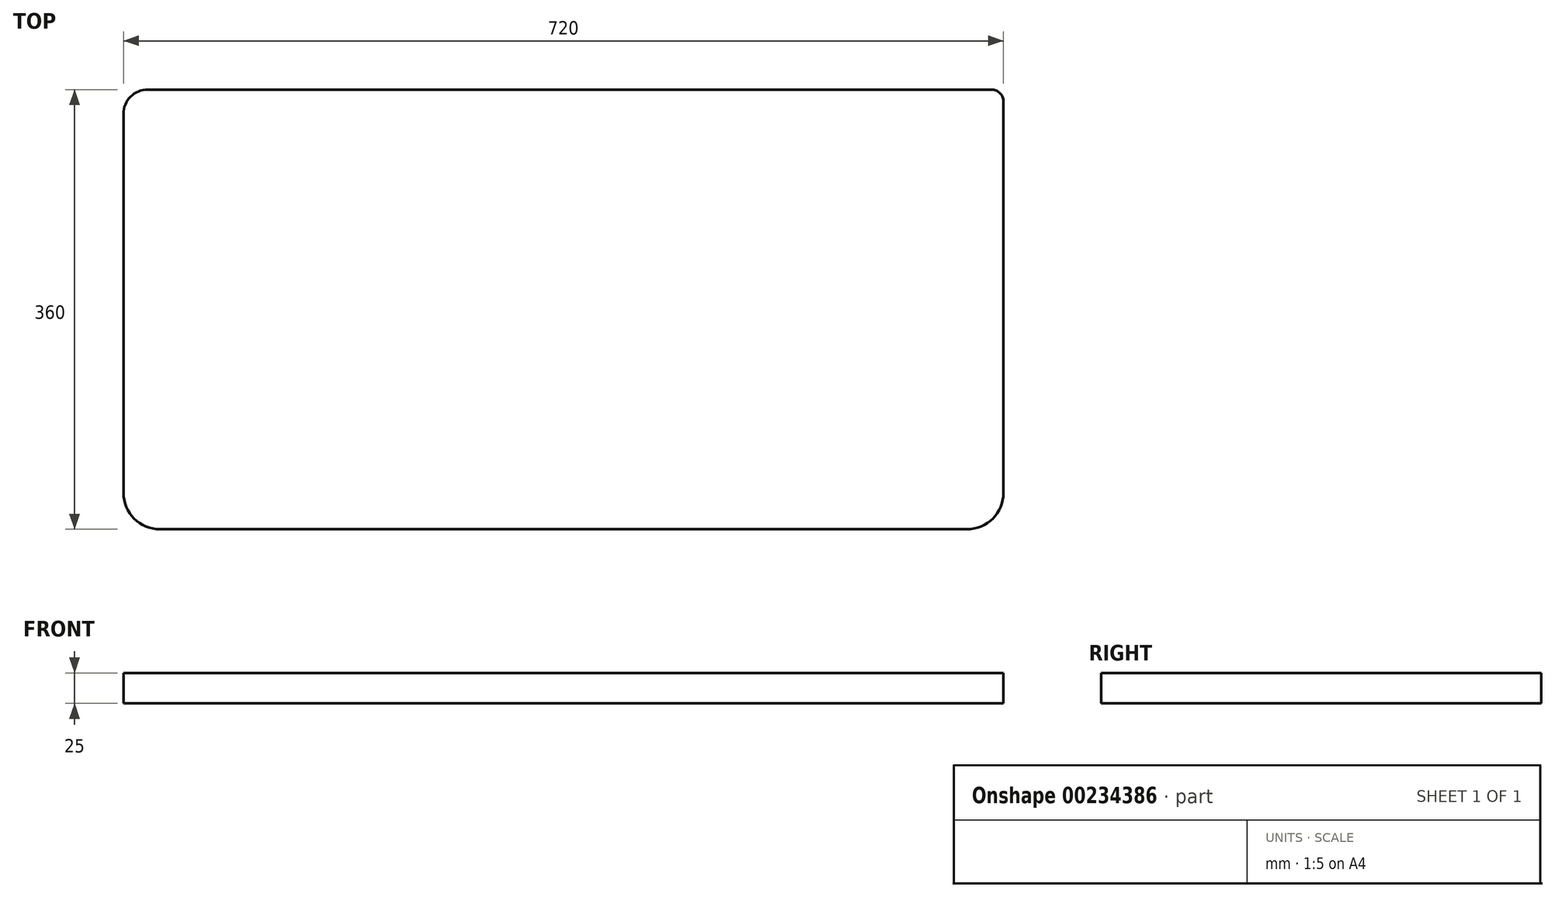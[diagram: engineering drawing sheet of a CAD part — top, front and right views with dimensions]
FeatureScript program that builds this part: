
annotation { "Feature Type Name" : "Feature", "Feature Type Description" : "" }
export const myFeature = defineFeature(function(context is Context, id is Id, definition is map)
    precondition{}
    {
        {
            var Q0;
            Q0=qCreatedBy(makeId("Top.planeOp"),FACE);
            var sketch = newSketch(context, id + "F0", { "sketchPlane" : qUnion([Q0])});
            skLineSegment(sketch, "E0.bottom", {"start": v(-340, 180) * mm, "end": v(350, 180) * mm});
            skLineSegment(sketch, "E0.top", {"start": v(-330, -180) * mm, "end": v(330, -180) * mm});
            skLineSegment(sketch, "E0.left", {"start": v(-360, 160) * mm, "end": v(-360, -150) * mm});
            skLineSegment(sketch, "E0.right", {"start": v(360, 170) * mm, "end": v(360, -150) * mm});
            skPoint(sketch, "E0.middle", {"position": v(0, 0) * mm});
            skPoint(sketch, "E1.visualSharp", {"position": v(-360, -180) * mm});
            skArc(sketch, "E1.filletArc", {"start": v(-360, -150) * mm, "mid": v(-351.21, -171.21) * mm, "end": v(-330, -180) * mm});
            skPoint(sketch, "E2.visualSharp", {"position": v(360, -180) * mm});
            skArc(sketch, "E2.filletArc", {"start": v(330, -180) * mm, "mid": v(351.21, -171.21) * mm, "end": v(360, -150) * mm});
            skPoint(sketch, "E3.visualSharp", {"position": v(-360, 180) * mm});
            skArc(sketch, "E3.filletArc", {"start": v(-340, 180) * mm, "mid": v(-354.14, 174.14) * mm, "end": v(-360, 160) * mm});
            skPoint(sketch, "E4.visualSharp", {"position": v(360, 180) * mm});
            skArc(sketch, "E4.filletArc", {"start": v(360, 170) * mm, "mid": v(357.07, 177.07) * mm, "end": v(350, 180) * mm});
            skSolve(sketch);
        }
        {
            var Q0;
            Q0 = qSketchRegion(id + "F0", true);
            extrude(context, id + "F1", {"entities" : qUnion([Q0]), "depth" : 25 * mm});
        }
    });
